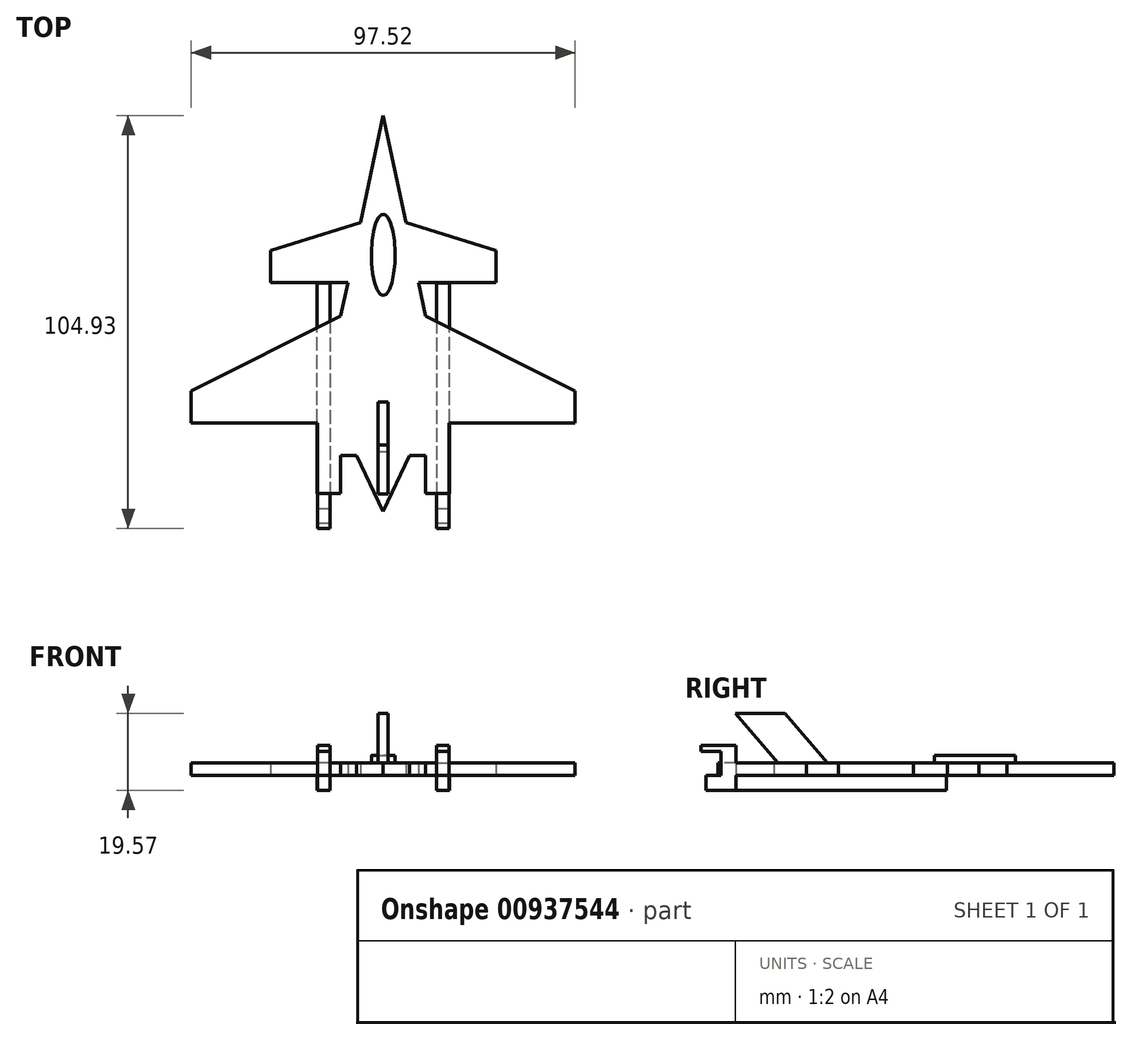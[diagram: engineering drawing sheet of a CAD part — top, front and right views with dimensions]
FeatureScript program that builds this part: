
annotation { "Feature Type Name" : "Feature", "Feature Type Description" : "" }
export const myFeature = defineFeature(function(context is Context, id is Id, definition is map)
    precondition{}
    {
        {
            var Q0;
            Q0=qCreatedBy(makeId("Top.planeOp"),FACE);
            var sketch = newSketch(context, id + "F0", { "sketchPlane" : qUnion([Q0])});
            skLineSegment(sketch, "E0", {"start": v(0, 0) * mm, "end": v(0, 50.97) * mm});
            skLineSegment(sketch, "E1", {"start": v(0, 50.97) * mm, "end": v(-10.78, 0) * mm});
            skLineSegment(sketch, "E2", {"start": v(-10.78, 0) * mm, "end": v(0, 0) * mm});
            skLineSegment(sketch, "E3.MirrorCS", {"start": v(0, 50.97) * mm, "end": v(10.78, 0) * mm});
            skLineSegment(sketch, "E4.MirrorCS", {"start": v(10.78, 0) * mm, "end": v(0, 0) * mm});
            skLineSegment(sketch, "E5", {"start": v(-10.78, 0) * mm, "end": v(-10.78, -35.49) * mm});
            skLineSegment(sketch, "E6", {"start": v(-10.78, -35.49) * mm, "end": v(-6.73, -35.49) * mm});
            skLineSegment(sketch, "E7", {"start": v(-6.73, -35.49) * mm, "end": v(0, -49.68) * mm});
            skLineSegment(sketch, "E8", {"start": v(0, -49.68) * mm, "end": v(0, 0) * mm});
            skLineSegment(sketch, "E9.MirrorCS", {"start": v(10.78, 0) * mm, "end": v(10.78, -35.49) * mm});
            skLineSegment(sketch, "E10.MirrorCS", {"start": v(10.78, -35.49) * mm, "end": v(6.73, -35.49) * mm});
            skLineSegment(sketch, "E11.MirrorCS", {"start": v(6.73, -35.49) * mm, "end": v(0, -49.68) * mm});
            skLineSegment(sketch, "E12", {"start": v(-10.78, -27.2) * mm, "end": v(-48.76, -27.2) * mm});
            skLineSegment(sketch, "E13", {"start": v(-48.76, -27.2) * mm, "end": v(-48.76, -19.08) * mm});
            skLineSegment(sketch, "E14", {"start": v(-48.76, -19.08) * mm, "end": v(-10.78, 0) * mm});
            skLineSegment(sketch, "E15.MirrorCS", {"start": v(48.76, -19.08) * mm, "end": v(10.78, 0) * mm});
            skLineSegment(sketch, "E16.MirrorCS", {"start": v(48.76, -27.2) * mm, "end": v(48.76, -19.08) * mm});
            skLineSegment(sketch, "E17.MirrorCS", {"start": v(10.78, -27.2) * mm, "end": v(48.76, -27.2) * mm});
            skLineSegment(sketch, "E18", {"start": v(-8.97, 8.58) * mm, "end": v(-28.67, 8.58) * mm});
            skLineSegment(sketch, "E19", {"start": v(-28.67, 8.58) * mm, "end": v(-28.67, 16.68) * mm});
            skLineSegment(sketch, "E20", {"start": v(-28.67, 16.68) * mm, "end": v(-5.76, 23.75) * mm});
            skLineSegment(sketch, "E21.MirrorCS", {"start": v(28.67, 16.68) * mm, "end": v(5.76, 23.75) * mm});
            skLineSegment(sketch, "E22.MirrorCS", {"start": v(28.67, 8.58) * mm, "end": v(28.67, 16.68) * mm});
            skLineSegment(sketch, "E23.MirrorCS", {"start": v(8.97, 8.58) * mm, "end": v(28.67, 8.58) * mm});
            skLineSegment(sketch, "E24", {"start": v(-10.78, -35.49) * mm, "end": v(-10.78, -45.07) * mm});
            skLineSegment(sketch, "E25", {"start": v(-10.78, -45.07) * mm, "end": v(-16.68, -45.07) * mm});
            skLineSegment(sketch, "E26", {"start": v(-16.68, -45.07) * mm, "end": v(-16.68, -27.2) * mm});
            skLineSegment(sketch, "E27.MirrorCS", {"start": v(10.78, -35.49) * mm, "end": v(10.78, -45.07) * mm});
            skLineSegment(sketch, "E28.MirrorCS", {"start": v(10.78, -45.07) * mm, "end": v(16.68, -45.07) * mm});
            skLineSegment(sketch, "E29.MirrorCS", {"start": v(16.68, -45.07) * mm, "end": v(16.68, -27.2) * mm});
            skSolve(sketch);
        }
        {
            var Q0;
            Q0 = qSketchRegion(id + "F0", true);
            extrude(context, id + "F1", {"entities" : qUnion([Q0]), "depth" : 3.17 * mm, "offsetDistance" : 25.4 * mm});
        }
        {
            var Q0;
            Q0=qCreatedBy(makeId("Top.planeOp"),FACE);
            var sketch = newSketch(context, id + "F2", { "sketchPlane" : qUnion([Q0])});
            skEllipse(sketch, "E30", {"center": v(0, 15.58) * mm, "majorRadius": 10.32 * mm, "minorRadius": 3.02 * mm, "majorAxis": v(0, -1)});
            skSolve(sketch);
        }
        {
            var Q0;
            Q0 = qSketchRegion(id + "F2", true);
            extrude(context, id + "F3", {"entities" : qUnion([Q0]), "operationType" : NewBodyOperationType.ADD, "depth" : 5.08 * mm, "offsetDistance" : 25.4 * mm});
        }
        {
            var Q0;
            Q0=qCreatedBy(makeId("Top.planeOp"),FACE);
            var sketch = newSketch(context, id + "F4", { "sketchPlane" : qUnion([Q0])});
            skLineSegment(sketch, "E31", {"start": v(-16.87, -45.07) * mm, "end": v(-16.87, 8.39) * mm});
            skLineSegment(sketch, "E32", {"start": v(-16.87, 8.39) * mm, "end": v(-13.55, 8.39) * mm});
            skLineSegment(sketch, "E33", {"start": v(-13.55, 8.39) * mm, "end": v(-13.55, -45.07) * mm});
            skLineSegment(sketch, "E34", {"start": v(-13.55, -45.07) * mm, "end": v(-16.87, -45.07) * mm});
            skLineSegment(sketch, "E35.MirrorCS", {"start": v(13.55, 8.39) * mm, "end": v(13.55, -45.07) * mm});
            skLineSegment(sketch, "E36.MirrorCS", {"start": v(16.87, -45.07) * mm, "end": v(16.87, 8.39) * mm});
            skLineSegment(sketch, "E37.MirrorCS", {"start": v(13.55, -45.07) * mm, "end": v(16.87, -45.07) * mm});
            skLineSegment(sketch, "E38.MirrorCS", {"start": v(16.87, 8.39) * mm, "end": v(13.55, 8.39) * mm});
            skSolve(sketch);
        }
        {
            var Q0;
            Q0 = qSketchRegion(id + "F4", true);
            extrude(context, id + "F5", {"entities" : qUnion([Q0]), "operationType" : NewBodyOperationType.ADD, "depth" : -3.8 * mm, "offsetDistance" : 25.4 * mm});
        }
        {
            var Q0;
            Q0=qCreatedBy(makeId("Right.planeOp"),FACE);
            var sketch = newSketch(context, id + "F6", { "sketchPlane" : qUnion([Q0])});
            skLineSegment(sketch, "E39", {"start": v(-33.42, 2.02) * mm, "end": v(-45.26, 15.76) * mm});
            skLineSegment(sketch, "E40", {"start": v(-32.72, 15.76) * mm, "end": v(-21, 2.16) * mm});
            skLineSegment(sketch, "E41", {"start": v(-21, 2.16) * mm, "end": v(-32.72, 15.76) * mm});
            skLineSegment(sketch, "E42", {"start": v(-45.26, 15.76) * mm, "end": v(-32.72, 15.76) * mm});
            skLineSegment(sketch, "E43", {"start": v(-33.42, 2.02) * mm, "end": v(-21, 2.16) * mm});
            skSolve(sketch);
        }
        {
            var Q0;
            Q0 = qSketchRegion(id + "F6", true);
            extrude(context, id + "F7", {"entities" : qUnion([Q0]), "operationType" : NewBodyOperationType.ADD, "depth" : 1.27 * mm, "offsetDistance" : 25.4 * mm, "hasSecondDirection" : true, "secondDirectionOppositeDirection" : true, "secondDirectionDepth" : 1.27 * mm});
        }
        {
            var Q0;
            Q0=makeQuery(id+"F5.boolean.opBoolean","MERGE",FACE,{"derivedFrom":[makeQuery(id+"F1.opExtrude","SWEPT_FACE",FACE,{"disambiguationData":[OSD([sQuery(id+"F0.wireOp",EDGE,"E25")])]}),makeQuery(id+"F5.opExtrude","SWEPT_FACE",FACE,{"disambiguationData":[OSD([sQuery(id+"F4.wireOp",EDGE,"E34")])]})]});
            var sketch = newSketch(context, id + "F8", { "sketchPlane" : qUnion([Q0])});
            skLineSegment(sketch, "E44.bottom", {"start": v(-16.68, 0) * mm, "end": v(-13.55, 0) * mm});
            skLineSegment(sketch, "E44.top", {"start": v(-16.68, -3.81) * mm, "end": v(-13.55, -3.81) * mm});
            skLineSegment(sketch, "E44.left", {"start": v(-16.68, 0) * mm, "end": v(-16.68, -3.81) * mm});
            skLineSegment(sketch, "E44.right", {"start": v(-13.55, 0) * mm, "end": v(-13.55, -3.81) * mm});
            skSolve(sketch);
        }
        {
            var Q0;
            Q0=makeQuery(id+"F5.boolean.opBoolean","MERGE",FACE,{"derivedFrom":[makeQuery(id+"F1.opExtrude","SWEPT_FACE",FACE,{"disambiguationData":[OSD([sQuery(id+"F0.wireOp",EDGE,"E28.MirrorCS")])]}),makeQuery(id+"F5.opExtrude","SWEPT_FACE",FACE,{"disambiguationData":[OSD([sQuery(id+"F4.wireOp",EDGE,"E37.MirrorCS")])]})]});
            var sketch = newSketch(context, id + "F9", { "sketchPlane" : qUnion([Q0])});
            skLineSegment(sketch, "E45.bottom", {"start": v(16.68, 0) * mm, "end": v(13.55, 0) * mm});
            skLineSegment(sketch, "E45.top", {"start": v(16.68, -3.81) * mm, "end": v(13.55, -3.81) * mm});
            skLineSegment(sketch, "E45.left", {"start": v(16.68, 0) * mm, "end": v(16.68, -3.81) * mm});
            skLineSegment(sketch, "E45.right", {"start": v(13.55, 0) * mm, "end": v(13.55, -3.81) * mm});
            skSolve(sketch);
        }
        {
            var Q0;
            Q0 = qSketchRegion(id + "F8", true);
            var Q1;
            Q1 = qSketchRegion(id + "F9", true);
            extrude(context, id + "F10", {"entities" : qUnion([Q0, Q1]), "operationType" : NewBodyOperationType.ADD, "depth" : 7.62 * mm, "offsetDistance" : 25.4 * mm});
        }
        {
            var Q0;
            Q0=makeQuery(id+"F10.opExtrude","SWEPT_FACE",FACE,{"disambiguationData":[OSD([sQuery(id+"F8.wireOp",EDGE,"E44.bottom")])]});
            var sketch = newSketch(context, id + "F11", { "sketchPlane" : qUnion([Q0])});
            skLineSegment(sketch, "E46", {"start": v(-16.68, -48.88) * mm, "end": v(-13.55, -48.88) * mm});
            skSolve(sketch);
        }
        {
            var Q0;
            Q0=makeQuery(id+"F10.opExtrude","SWEPT_FACE",FACE,{"disambiguationData":[OSD([sQuery(id+"F9.wireOp",EDGE,"E45.bottom")])]});
            var sketch = newSketch(context, id + "F12", { "sketchPlane" : qUnion([Q0])});
            skLineSegment(sketch, "E47", {"start": v(13.55, -48.88) * mm, "end": v(16.68, -48.88) * mm});
            skSolve(sketch);
        }
        {
            var Q0;
            {var subQ0=sQuery(id+"F11.wireOp",EDGE,"E46");Q0=makeQuery(id+"F11.imprint","IMPRINT",FACE,{"disambiguationData":[TD([[makeQuery(id+"F11.imprint","IMPRINT",EDGE,{"derivedFrom":subQ0}),1.0]])]});}
            var Q1;
            {var subQ0=sQuery(id+"F12.wireOp",EDGE,"E47");Q1=makeQuery(id+"F12.imprint","IMPRINT",FACE,{"disambiguationData":[TD([[makeQuery(id+"F12.imprint","IMPRINT",EDGE,{"derivedFrom":subQ0}),1.0]])]});}
            extrude(context, id + "F13", {"entities" : qUnion([Q0, Q1]), "operationType" : NewBodyOperationType.ADD, "depth" : 7.62 * mm, "offsetDistance" : 25.4 * mm});
        }
        {
            var Q0;
            Q0=makeQuery(id+"F13.opExtrude","SWEPT_FACE",FACE,{"disambiguationData":[OSD([sQuery(id+"F11.wireOp",EDGE,"E46")])]});
            var sketch = newSketch(context, id + "F14", { "sketchPlane" : qUnion([Q0])});
            skLineSegment(sketch, "E48", {"start": v(-16.68, 6.15) * mm, "end": v(-13.55, 6.15) * mm});
            skSolve(sketch);
        }
        {
            var Q0;
            Q0=makeQuery(id+"F13.opExtrude","SWEPT_FACE",FACE,{"disambiguationData":[OSD([sQuery(id+"F12.wireOp",EDGE,"E47")])]});
            var sketch = newSketch(context, id + "F15", { "sketchPlane" : qUnion([Q0])});
            skLineSegment(sketch, "E49", {"start": v(13.55, 6.1) * mm, "end": v(16.68, 6.1) * mm});
            skSolve(sketch);
        }
        {
            var Q0;
            {var subQ0=sQuery(id+"F15.wireOp",EDGE,"E49");Q0=makeQuery(id+"F15.imprint","IMPRINT",FACE,{"disambiguationData":[TD([[makeQuery(id+"F15.imprint","IMPRINT",EDGE,{"derivedFrom":subQ0}),1.0]])]});}
            var Q1;
            {var subQ0=sQuery(id+"F14.wireOp",EDGE,"E48");Q1=makeQuery(id+"F14.imprint","IMPRINT",FACE,{"disambiguationData":[TD([[makeQuery(id+"F14.imprint","IMPRINT",EDGE,{"derivedFrom":subQ0}),1.0]])]});}
            extrude(context, id + "F16", {"entities" : qUnion([Q0, Q1]), "operationType" : NewBodyOperationType.ADD, "depth" : 5.08 * mm, "offsetDistance" : 25.4 * mm});
        }
    });
